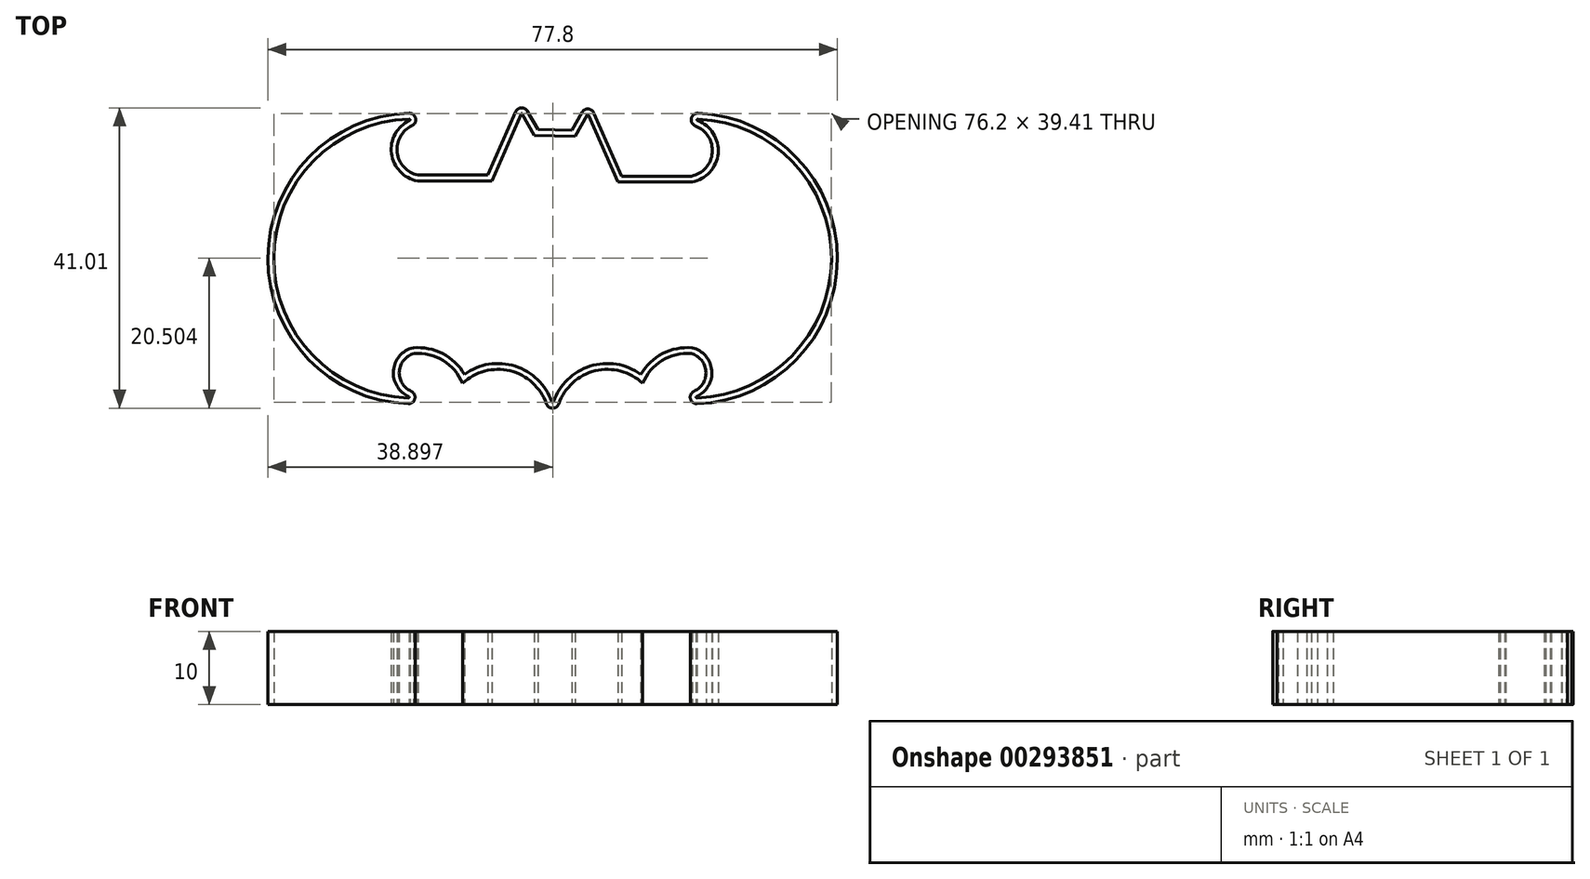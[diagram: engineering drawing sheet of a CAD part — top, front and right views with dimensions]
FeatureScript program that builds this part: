
annotation { "Feature Type Name" : "Feature", "Feature Type Description" : "" }
export const myFeature = defineFeature(function(context is Context, id is Id, definition is map)
    precondition{}
    {
        {
            var Q0;
            Q0=qCreatedBy(makeId("Top.planeOp"),FACE);
            var sketch = newSketch(context, id + "F0", { "sketchPlane" : qUnion([Q0])});
            skArc(sketch, "E0", {"start": v(-14, 19.19) * mm, "mid": v(-32.51, 0.2) * mm, "end": v(-14.11, -18.9) * mm});
            skArc(sketch, "E1", {"start": v(25.28, -18.9) * mm, "mid": v(43.69, 0.08) * mm, "end": v(25.43, 19.18) * mm});
            skArc(sketch, "E2", {"start": v(-13.96, 19) * mm, "mid": v(-16.43, 14.48) * mm, "end": v(-12.89, 10.74) * mm});
            skArc(sketch, "E3.MirrorCS", {"start": v(25.39, 18.99) * mm, "mid": v(28.2, 14.5) * mm, "end": v(24.64, 10.6) * mm});
            skArc(sketch, "E4", {"start": v(-13.46, -12.05) * mm, "mid": v(-16.16, -15.16) * mm, "end": v(-14.07, -18.7) * mm});
            skArc(sketch, "E5.MirrorCS", {"start": v(24.64, -12.05) * mm, "mid": v(27.33, -15.16) * mm, "end": v(25.24, -18.7) * mm});
            skArc(sketch, "E6", {"start": v(-6.45, -15.66) * mm, "mid": v(-9.43, -12.85) * mm, "end": v(-13.46, -12.05) * mm});
            skArc(sketch, "E7", {"start": v(5.5, -19.43) * mm, "mid": v(0.46, -14.56) * mm, "end": v(-6.45, -15.66) * mm});
            skArc(sketch, "E8.MirrorCS", {"start": v(5.68, -19.43) * mm, "mid": v(10.71, -14.56) * mm, "end": v(17.62, -15.66) * mm});
            skArc(sketch, "E9.MirrorCS", {"start": v(17.62, -15.66) * mm, "mid": v(20.6, -12.85) * mm, "end": v(24.64, -12.05) * mm});
            skLineSegment(sketch, "E10", {"start": v(-12.89, 10.74) * mm, "end": v(-2.73, 10.74) * mm});
            skLineSegment(sketch, "E11", {"start": v(-2.73, 10.74) * mm, "end": v(1.27, 19.86) * mm});
            skLineSegment(sketch, "E12", {"start": v(1.45, 19.87) * mm, "end": v(3.1, 16.98) * mm});
            skLineSegment(sketch, "E13.MirrorCS", {"start": v(10.3, 19.72) * mm, "end": v(8.65, 16.83) * mm});
            skLineSegment(sketch, "E14.MirrorCS", {"start": v(14.48, 10.6) * mm, "end": v(10.48, 19.71) * mm});
            skLineSegment(sketch, "E15.MirrorCS", {"start": v(24.64, 10.6) * mm, "end": v(14.48, 10.6) * mm});
            skLineSegment(sketch, "E16", {"start": v(3.1, 16.98) * mm, "end": v(8.65, 16.83) * mm});
            skPoint(sketch, "E17.visualSharp", {"position": v(5.59, -19.7) * mm});
            skArc(sketch, "E17.filletArc", {"start": v(5.5, -19.43) * mm, "mid": v(5.59, -19.5) * mm, "end": v(5.68, -19.43) * mm});
            skPoint(sketch, "E18.visualSharp", {"position": v(24.64, -18.9) * mm});
            skArc(sketch, "E18.filletArc", {"start": v(25.24, -18.7) * mm, "mid": v(25.18, -18.81) * mm, "end": v(25.28, -18.9) * mm});
            skPoint(sketch, "E19.visualSharp", {"position": v(-13.46, -18.9) * mm});
            skArc(sketch, "E19.filletArc", {"start": v(-14.11, -18.9) * mm, "mid": v(-14, -18.81) * mm, "end": v(-14.07, -18.7) * mm});
            skPoint(sketch, "E20.visualSharp", {"position": v(24.64, 19.2) * mm});
            skArc(sketch, "E20.filletArc", {"start": v(25.43, 19.18) * mm, "mid": v(25.32, 19.1) * mm, "end": v(25.39, 18.99) * mm});
            skPoint(sketch, "E21.visualSharp", {"position": v(-13.46, 19.2) * mm});
            skArc(sketch, "E21.filletArc", {"start": v(-13.96, 19) * mm, "mid": v(-13.9, 19.11) * mm, "end": v(-14, 19.19) * mm});
            skPoint(sketch, "E22.visualSharp", {"position": v(1.35, 20.04) * mm});
            skArc(sketch, "E22.filletArc", {"start": v(1.45, 19.87) * mm, "mid": v(1.35, 19.92) * mm, "end": v(1.27, 19.86) * mm});
            skPoint(sketch, "E23.visualSharp", {"position": v(10.4, 19.9) * mm});
            skArc(sketch, "E23.filletArc", {"start": v(10.48, 19.71) * mm, "mid": v(10.4, 19.77) * mm, "end": v(10.3, 19.72) * mm});
            skArc(sketch, "E24.0", {"start": v(4.74, -19.7) * mm, "mid": v(5.59, -20.3) * mm, "end": v(6.44, -19.7) * mm});
            skLineSegment(sketch, "E24.1", {"start": v(2.14, 20.27) * mm, "end": v(3.57, 17.77) * mm});
            skArc(sketch, "E24.2", {"start": v(2.14, 20.27) * mm, "mid": v(1.31, 20.72) * mm, "end": v(0.54, 20.18) * mm});
            skLineSegment(sketch, "E24.3", {"start": v(-3.25, 11.54) * mm, "end": v(0.54, 20.18) * mm});
            skLineSegment(sketch, "E24.4", {"start": v(-12.81, 11.54) * mm, "end": v(-3.25, 11.54) * mm});
            skArc(sketch, "E24.5", {"start": v(-13.62, 18.28) * mm, "mid": v(-15.64, 14.62) * mm, "end": v(-12.81, 11.54) * mm});
            skArc(sketch, "E24.6", {"start": v(-13.62, 18.28) * mm, "mid": v(-13.13, 19.3) * mm, "end": v(-14.03, 19.99) * mm});
            skArc(sketch, "E24.7", {"start": v(-6.71, -16.91) * mm, "mid": v(-9.36, -13.8) * mm, "end": v(-13.33, -12.84) * mm});
            skArc(sketch, "E24.8", {"start": v(-13.33, -12.84) * mm, "mid": v(-15.36, -15.26) * mm, "end": v(-13.75, -17.97) * mm});
            skArc(sketch, "E24.9", {"start": v(-14.14, -19.7) * mm, "mid": v(-13.23, -19) * mm, "end": v(-13.75, -17.97) * mm});
            skArc(sketch, "E24.10", {"start": v(-14.03, 19.99) * mm, "mid": v(-33.31, 0.2) * mm, "end": v(-14.14, -19.7) * mm});
            skLineSegment(sketch, "E24.11", {"start": v(3.57, 17.77) * mm, "end": v(8.2, 17.64) * mm});
            skArc(sketch, "E24.12", {"start": v(4.74, -19.7) * mm, "mid": v(-0.24, -15.2) * mm, "end": v(-6.71, -16.91) * mm});
            skLineSegment(sketch, "E24.13", {"start": v(9.6, 20.12) * mm, "end": v(8.2, 17.64) * mm});
            skArc(sketch, "E24.14", {"start": v(11.21, 20.03) * mm, "mid": v(10.44, 20.57) * mm, "end": v(9.6, 20.12) * mm});
            skLineSegment(sketch, "E24.15", {"start": v(15, 11.4) * mm, "end": v(11.21, 20.03) * mm});
            skLineSegment(sketch, "E24.16", {"start": v(24.56, 11.4) * mm, "end": v(15, 11.4) * mm});
            skArc(sketch, "E24.17", {"start": v(25.1, 18.24) * mm, "mid": v(27.4, 14.61) * mm, "end": v(24.56, 11.4) * mm});
            skArc(sketch, "E24.18", {"start": v(25.46, 19.98) * mm, "mid": v(24.54, 19.26) * mm, "end": v(25.1, 18.24) * mm});
            skArc(sketch, "E24.19", {"start": v(25.31, -19.7) * mm, "mid": v(44.49, 0.07) * mm, "end": v(25.46, 19.98) * mm});
            skArc(sketch, "E24.20", {"start": v(24.92, -17.97) * mm, "mid": v(24.4, -19) * mm, "end": v(25.31, -19.7) * mm});
            skArc(sketch, "E24.21", {"start": v(24.5, -12.84) * mm, "mid": v(26.54, -15.26) * mm, "end": v(24.92, -17.97) * mm});
            skArc(sketch, "E24.22", {"start": v(17.89, -16.91) * mm, "mid": v(20.54, -13.8) * mm, "end": v(24.5, -12.84) * mm});
            skArc(sketch, "E24.23", {"start": v(6.44, -19.7) * mm, "mid": v(11.4, -15.2) * mm, "end": v(17.89, -16.91) * mm});
            skSolve(sketch);
        }
        {
            var Q0;
            Q0=qSketchRegion(id+"F0",true);
            extrude(context, id + "F1", {"entities" : qUnion([Q0]), "depth" : 10 * mm});
        }
    });
